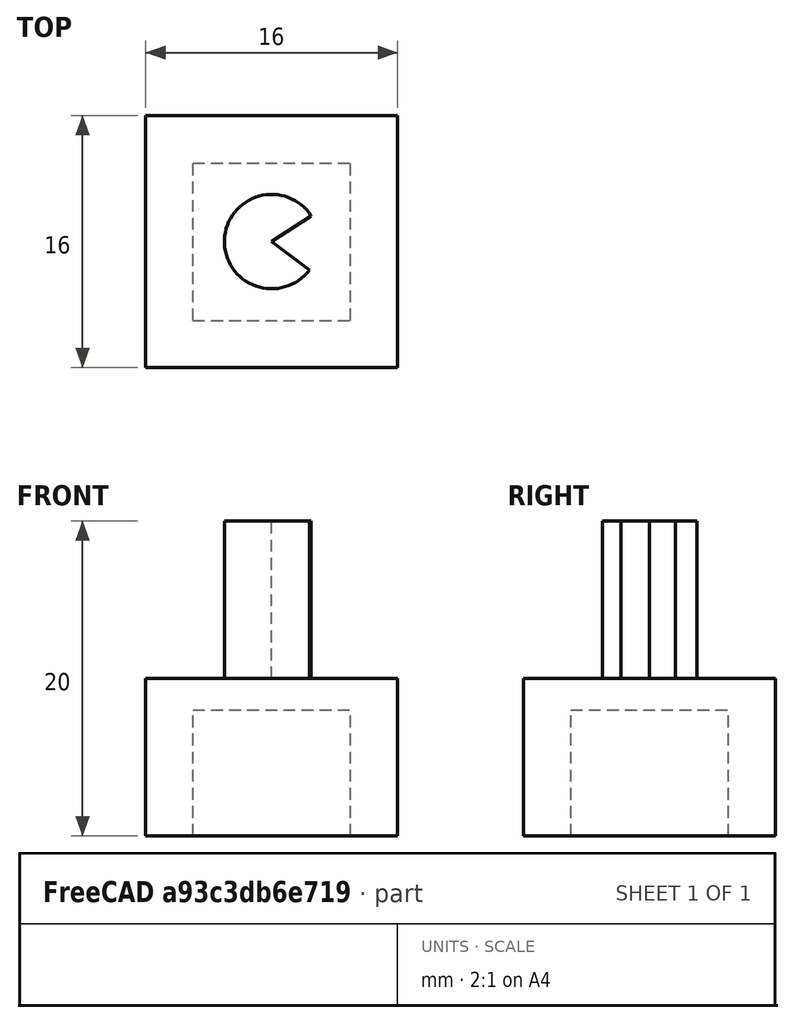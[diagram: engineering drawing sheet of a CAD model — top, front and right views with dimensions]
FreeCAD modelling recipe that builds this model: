
FCSTD DOCUMENT  (FreeCAD 0.18.3R)
Label: pacman
License: All rights reserved
LicenseURL: http://en.wikipedia.org/wiki/All_rights_reserved
objects: Part::Box×2, Part::Cylinder×1, Part::Fuse×1, Part::Cut×1
note: 5 computed .brp shape members not serialized (recipe doc carries the construction recipe); baked Part::Feature solids carry a one-line shape summary decoded from their .brp

FEATURE [Part::Box] Box  label="Cube"
  AttacherType = Attacher::AttachEngine3D
  Height = 10
  Length = 16
  Placement = pos=(-8,-8,0) rot=(0,0,1;0rad)
  Width = 16
FEATURE [Part::Cylinder] Cylinder
  Angle = 290
  AttacherType = Attacher::AttachEngine3D
  Height = 10
  Placement = pos=(0,0,10) rot=(0,0,1;0.575959rad)
  Radius = 3
FEATURE [Part::Fuse] Fusion
  Base = -> Box
  Tool = -> Cylinder
FEATURE [Part::Box] Box001  label="Cube001"
  AttacherType = Attacher::AttachEngine3D
  Height = 8
  Length = 10
  Placement = pos=(-5,-5,0) rot=(0,0,1;0rad)
  Width = 10
FEATURE [Part::Cut] Cut
  Base = -> Fusion
  Tool = -> Box001
